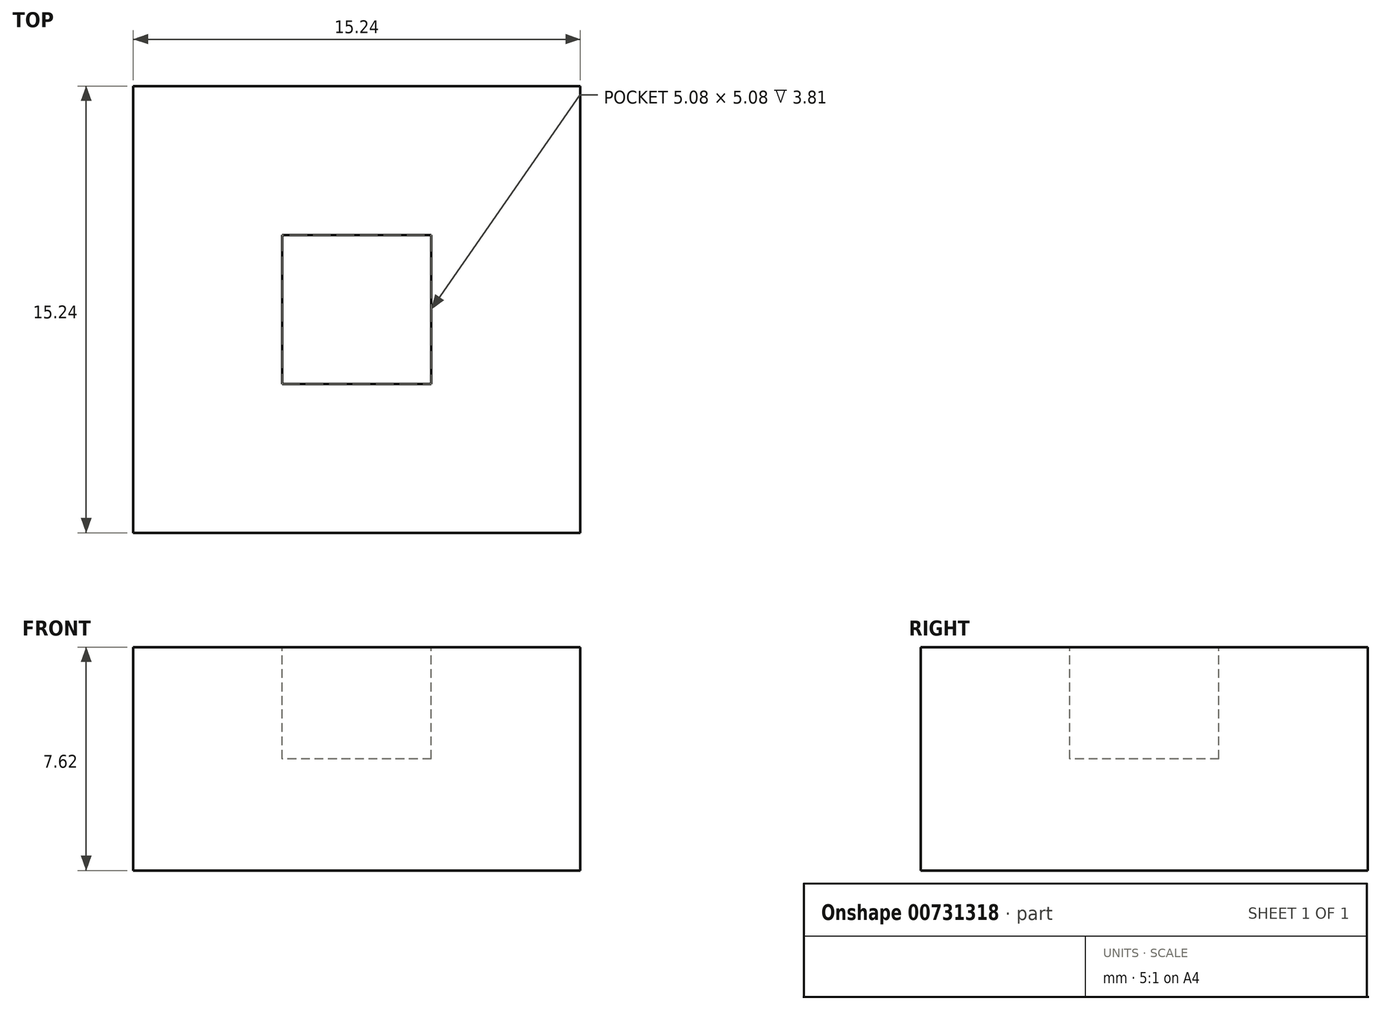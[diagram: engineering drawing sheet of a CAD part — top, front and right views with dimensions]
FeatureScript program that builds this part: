
annotation { "Feature Type Name" : "Feature", "Feature Type Description" : "" }
export const myFeature = defineFeature(function(context is Context, id is Id, definition is map)
    precondition{}
    {
        {
            var Q0;
            Q0=qCreatedBy(makeId("Top.planeOp"),FACE);
            var sketch = newSketch(context, id + "F0", { "sketchPlane" : qUnion([Q0])});
            skLineSegment(sketch, "E0", {"start": v(0, 0) * mm, "end": v(0, 15.24) * mm});
            skLineSegment(sketch, "E1", {"start": v(0, 15.24) * mm, "end": v(15.24, 15.24) * mm});
            skLineSegment(sketch, "E2", {"start": v(15.24, 15.24) * mm, "end": v(15.24, 0) * mm});
            skLineSegment(sketch, "E3", {"start": v(15.24, 0) * mm, "end": v(0, 0) * mm});
            skSolve(sketch);
        }
        {
            var Q0;
            Q0 = qSketchRegion(id + "F0", true);
            var Q1;
            Q1=makeQuery(id+"F0.imprint","IMPRINT",FACE,{"disambiguationData":[TD([[makeQuery(id+"F0.imprint","IMPRINT",EDGE,{"derivedFrom":sQuery(id+"F0.wireOp",EDGE,"E0")}),-1.0]])]});
            extrude(context, id + "F1", {"entities" : qUnion([Q0, Q1]), "depth" : 7.62 * mm, "offsetDistance" : 25.4 * mm});
        }
        {
            var Q0;
            Q0=makeQuery(id+"F1.opExtrude","CAP_FACE",FACE,{"disambiguationData":[OSD([sQuery(id+"F0.wireOp",EDGE,"E0"),sQuery(id+"F0.wireOp",EDGE,"E1"),sQuery(id+"F0.wireOp",EDGE,"E2"),sQuery(id+"F0.wireOp",EDGE,"E3")])],"isStart":false});
            var sketch = newSketch(context, id + "F2", { "sketchPlane" : qUnion([Q0])});
            skLineSegment(sketch, "E4", {"start": v(5.08, 10.16) * mm, "end": v(5.08, 5.08) * mm});
            skLineSegment(sketch, "E5", {"start": v(5.08, 5.08) * mm, "end": v(10.16, 5.08) * mm});
            skLineSegment(sketch, "E6", {"start": v(10.16, 5.08) * mm, "end": v(10.16, 10.16) * mm});
            skLineSegment(sketch, "E7", {"start": v(10.16, 10.16) * mm, "end": v(5.08, 10.16) * mm});
            skSolve(sketch);
        }
        {
            var Q0;
            Q0=makeQuery(id+"F2.imprint","IMPRINT",FACE,{"disambiguationData":[TD([[makeQuery(id+"F2.imprint","IMPRINT",EDGE,{"derivedFrom":sQuery(id+"F2.wireOp",EDGE,"E4")}),1.0]])]});
            extrude(context, id + "F3", {"entities" : qUnion([Q0]), "operationType" : NewBodyOperationType.REMOVE, "oppositeDirection" : true, "depth" : 3.8 * mm, "offsetDistance" : 25.4 * mm});
        }
    });
